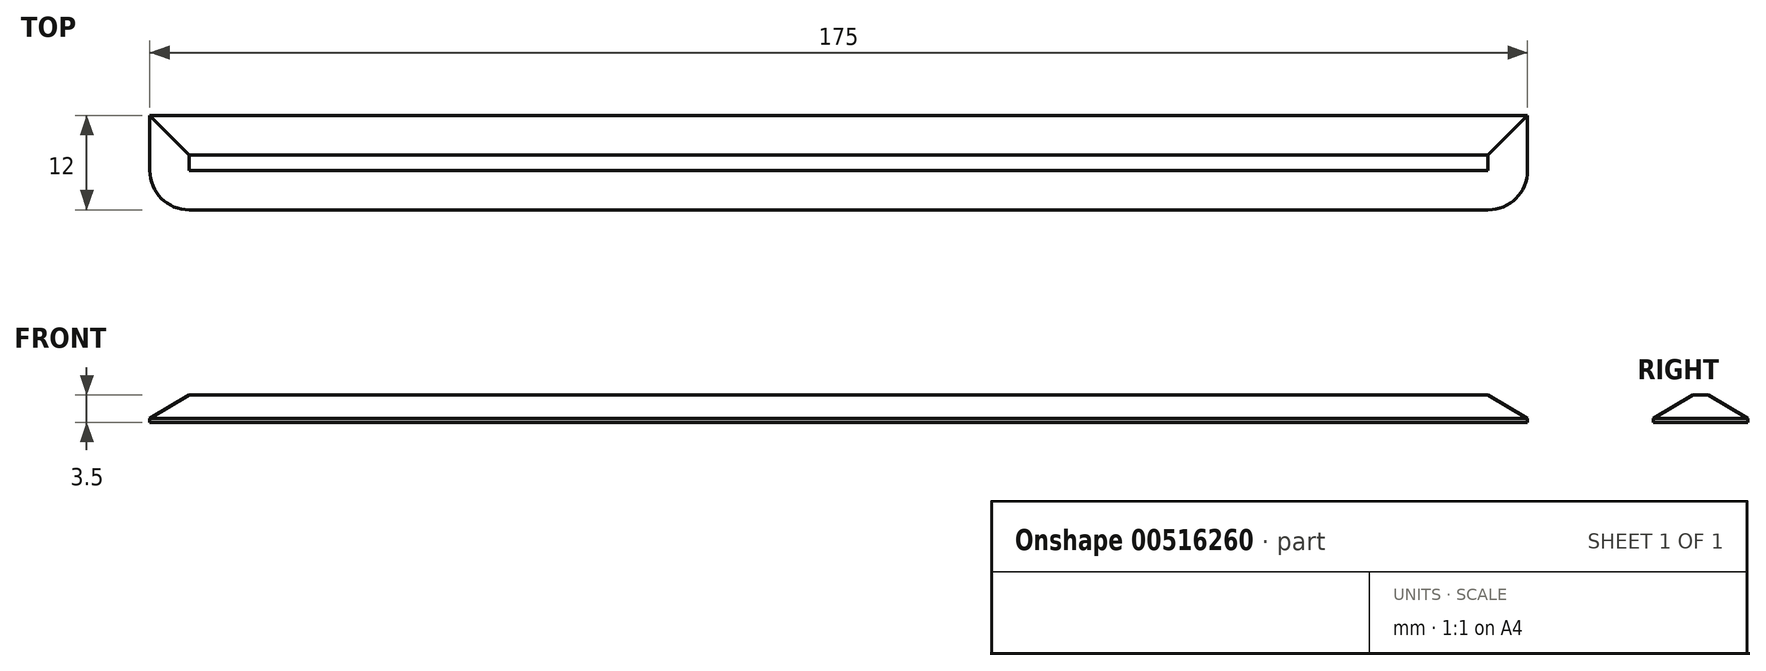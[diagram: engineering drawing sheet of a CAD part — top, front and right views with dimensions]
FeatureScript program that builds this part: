
annotation { "Feature Type Name" : "Feature", "Feature Type Description" : "" }
export const myFeature = defineFeature(function(context is Context, id is Id, definition is map)
    precondition{}
    {
        {
            var Q0;
            Q0=qCreatedBy(makeId("Top.planeOp"),FACE);
            var sketch = newSketch(context, id + "F0", { "sketchPlane" : qUnion([Q0])});
            skLineSegment(sketch, "E0.bottom", {"start": v(82.5, -6) * mm, "end": v(-82.5, -6) * mm});
            skLineSegment(sketch, "E0.top", {"start": v(87.5, 6) * mm, "end": v(-87.5, 6) * mm});
            skLineSegment(sketch, "E0.left", {"start": v(87.5, -1) * mm, "end": v(87.5, 6) * mm});
            skLineSegment(sketch, "E0.right", {"start": v(-87.5, -1) * mm, "end": v(-87.5, 6) * mm});
            skPoint(sketch, "E0.middle", {"position": v(0, 0) * mm});
            skPoint(sketch, "E1.visualSharp", {"position": v(-87.5, -6) * mm});
            skArc(sketch, "E1.filletArc", {"start": v(-87.5, -1) * mm, "mid": v(-86.04, -4.54) * mm, "end": v(-82.5, -6) * mm});
            skPoint(sketch, "E2.visualSharp", {"position": v(87.5, -6) * mm});
            skArc(sketch, "E2.filletArc", {"start": v(82.5, -6) * mm, "mid": v(86.04, -4.54) * mm, "end": v(87.5, -1) * mm});
            skSolve(sketch);
        }
        {
            var Q0;
            Q0=makeQuery(id+"F0.imprint","IMPRINT",FACE,{"disambiguationData":[TD([[makeQuery(id+"F0.imprint","IMPRINT",EDGE,{"derivedFrom":sQuery(id+"F0.wireOp",EDGE,"E0.bottom")}),-1.0]])]});
            extrude(context, id + "F1", {"entities" : qUnion([Q0]), "depth" : 3.5 * mm, "offsetDistance" : 25 * mm});
        }
        {
            var Q0;
            Q0=makeQuery(id+"F1.opExtrude","CAP_EDGE",EDGE,{"disambiguationData":[OSD([sQuery(id+"F0.wireOp",EDGE,"E0.top")])],"isStart":false});
            var Q1;
            Q1=makeQuery(id+"F1.opExtrude","CAP_EDGE",EDGE,{"disambiguationData":[OSD([sQuery(id+"F0.wireOp",EDGE,"E0.left")])],"isStart":false});
            chamfer(context, id + "F2", {"entities" : qUnion([Q0, Q1]), "chamferType" : ChamferType.TWO_OFFSETS, "width1" : 5 * mm, "oppositeDirection" : false, "width2" : 3 * mm, "tangentPropagation" : true});
        }
    });
